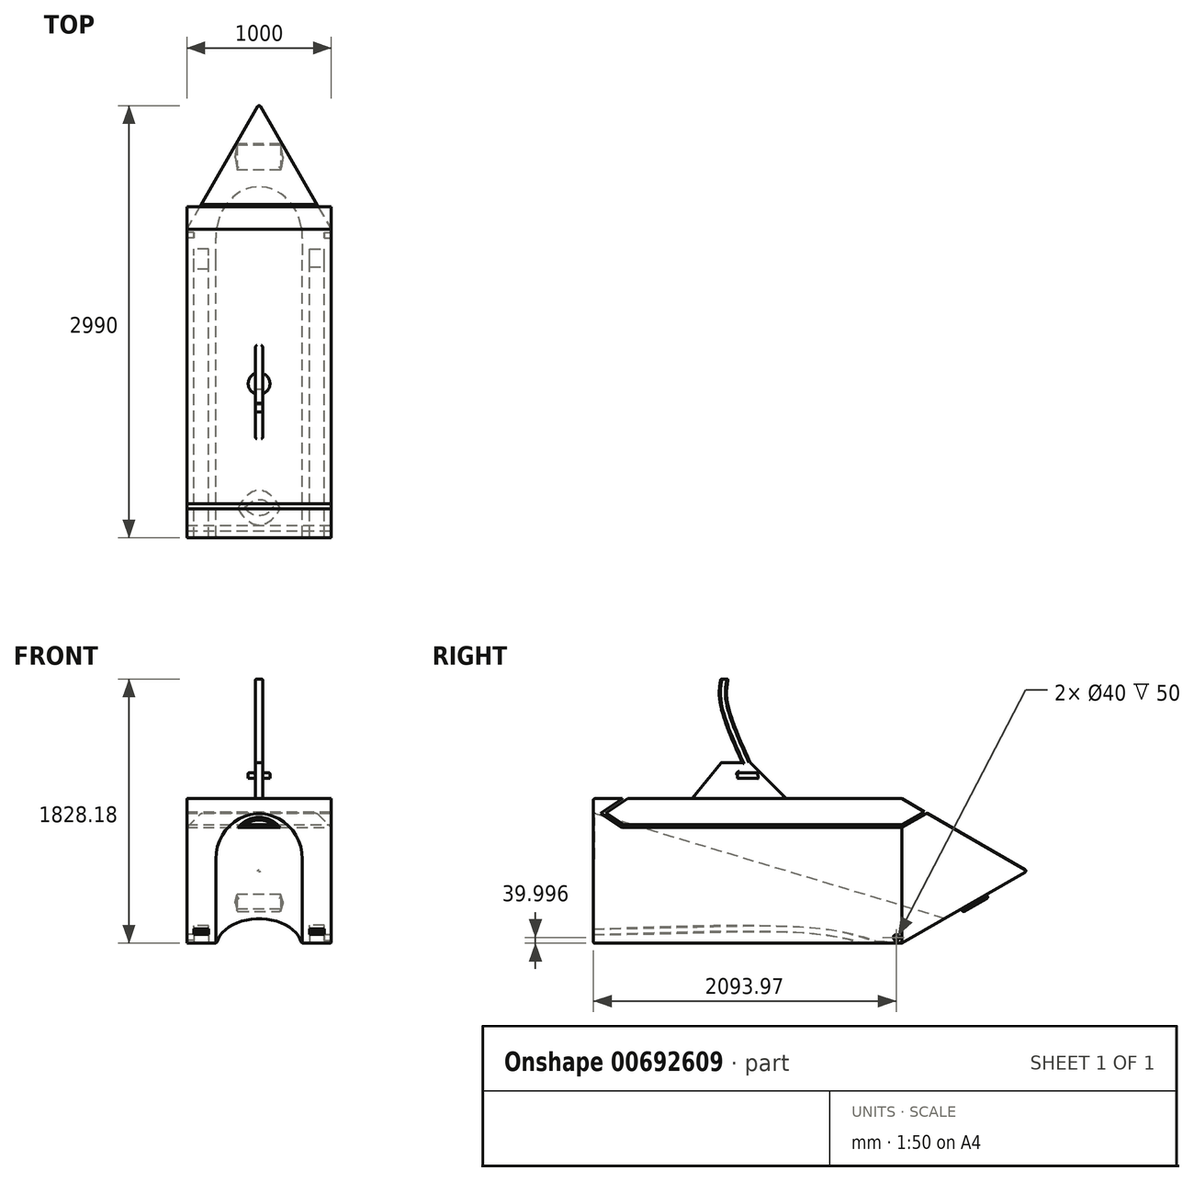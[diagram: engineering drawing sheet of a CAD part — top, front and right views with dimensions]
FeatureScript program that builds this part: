
annotation { "Feature Type Name" : "Feature", "Feature Type Description" : "" }
export const myFeature = defineFeature(function(context is Context, id is Id, definition is map)
    precondition{}
    {
        {
            var Q0;
            Q0=qCreatedBy(makeId("Front.planeOp"),FACE);
            var sketch = newSketch(context, id + "F0", { "sketchPlane" : qUnion([Q0])});
            skLineSegment(sketch, "E0.bottom", {"start": v(-515.88, 678.78) * mm, "end": v(484.12, 678.78) * mm});
            skLineSegment(sketch, "E0.top", {"start": v(-515.88, -321.22) * mm, "end": v(484.12, -321.22) * mm});
            skLineSegment(sketch, "E0.left", {"start": v(-515.88, 678.78) * mm, "end": v(-515.88, -321.22) * mm});
            skLineSegment(sketch, "E0.right", {"start": v(484.12, 678.78) * mm, "end": v(484.12, -321.22) * mm});
            skSolve(sketch);
        }
        {
            var Q0;
            Q0 = qSketchRegion(id + "F0", true);
            extrude(context, id + "F1", {"entities" : qUnion([Q0]), "depth" : 3000 * mm, "offsetDistance" : 25 * mm});
        }
        {
            var Q0;
            Q0=makeQuery(id+"F1.opExtrude","SWEPT_FACE",FACE,{"disambiguationData":[OSD([sQuery(id+"F0.wireOp",EDGE,"E0.right")])]});
            var sketch = newSketch(context, id + "F2", { "sketchPlane" : qUnion([Q0])});
            skLineSegment(sketch, "E1", {"start": v(-3000, 678.78) * mm, "end": v(-3000, 578.78) * mm});
            skLineSegment(sketch, "E2", {"start": v(0, 678.78) * mm, "end": v(0, -321.22) * mm});
            skLineSegment(sketch, "E3", {"start": v(-3000, 578.78) * mm, "end": v(0, -321.22) * mm});
            skLineSegment(sketch, "E4", {"start": v(0, -321.22) * mm, "end": v(0, -321.22) * mm});
            skSolve(sketch);
        }
        {
            var Q0;
            {var subQ0=sQuery(id+"F2.wireOp",EDGE,"E3");Q0=makeQuery(id+"F2.imprint","IMPRINT",FACE,{"disambiguationData":[TD([[makeQuery(id+"F2.imprint","IMPRINT",EDGE,{"derivedFrom":subQ0}),-1.0]])]});}
            extrude(context, id + "F3", {"entities" : qUnion([Q0]), "operationType" : NewBodyOperationType.REMOVE, "oppositeDirection" : true, "depth" : 800 * mm, "offsetDistance" : 25 * mm});
        }
        {
            var Q0;
            Q0=makeQuery(id+"F1.opExtrude","SWEPT_FACE",FACE,{"disambiguationData":[OSD([sQuery(id+"F0.wireOp",EDGE,"E0.bottom")])]});
            var sketch = newSketch(context, id + "F4", { "sketchPlane" : qUnion([Q0])});
            skLineSegment(sketch, "E5.bottom", {"start": v(484.12, -3000) * mm, "end": v(284.12, -3000) * mm});
            skLineSegment(sketch, "E5.top", {"start": v(484.12, 0) * mm, "end": v(284.12, 0) * mm});
            skLineSegment(sketch, "E5.left", {"start": v(484.12, -3000) * mm, "end": v(484.12, 0) * mm});
            skLineSegment(sketch, "E5.right", {"start": v(284.12, -3000) * mm, "end": v(284.12, 0) * mm});
            skSolve(sketch);
        }
        {
            var Q0;
            Q0 = qSketchRegion(id + "F4", true);
            extrude(context, id + "F5", {"entities" : qUnion([Q0]), "operationType" : NewBodyOperationType.ADD, "oppositeDirection" : true, "depth" : 1000 * mm, "offsetDistance" : 25 * mm});
        }
        {
            var Q0;
            Q0=makeQuery(id+"F3.boolean.opBoolean","COPY",EDGE,{"derivedFrom":makeQuery(id+"F3.opExtrude","CAP_EDGE",EDGE,{"disambiguationData":[OSD([sQuery(id+"F2.wireOp",EDGE,"E3")])],"isStart":false})});
            var Q1;
            Q1=makeQuery(id+"F5.boolean.opBoolean","INTERSECT",EDGE,{"derivedFrom":[makeQuery(id+"F3.boolean.opBoolean","COPY",FACE,{"derivedFrom":makeQuery(id+"F3.opExtrude","SWEPT_FACE",FACE,{"disambiguationData":[OSD([sQuery(id+"F2.wireOp",EDGE,"E3")])]})}),makeQuery(id+"F5.opExtrude","SWEPT_FACE",FACE,{"disambiguationData":[OSD([sQuery(id+"F4.wireOp",EDGE,"E5.right")])]})]});
            fillet(context, id + "F6", {"entities" : qUnion([Q0, Q1]), "radius" : 300 * mm, "tangentPropagation" : true, "allowEdgeOverflow" : false});
        }
        {
            var Q0;
            Q0=makeQuery(id+"F5.boolean.opBoolean","MERGE",FACE,{"derivedFrom":[makeQuery(id+"F1.opExtrude","SWEPT_FACE",FACE,{"disambiguationData":[OSD([sQuery(id+"F0.wireOp",EDGE,"E0.right")])]}),makeQuery(id+"F5.opExtrude","SWEPT_FACE",FACE,{"disambiguationData":[OSD([sQuery(id+"F4.wireOp",EDGE,"E5.left")])]})]});
            var sketch = newSketch(context, id + "F7", { "sketchPlane" : qUnion([Q0])});
            skLineSegment(sketch, "E6", {"start": v(0, 178.78) * mm, "end": v(-866.03, 678.78) * mm});
            skLineSegment(sketch, "E7", {"start": v(-866.03, 678.78) * mm, "end": v(0, 678.78) * mm});
            skLineSegment(sketch, "E8", {"start": v(0, 678.78) * mm, "end": v(0, 178.78) * mm});
            skLineSegment(sketch, "E9", {"start": v(0, 178.78) * mm, "end": v(-866.03, -321.22) * mm});
            skLineSegment(sketch, "E10", {"start": v(-866.03, -321.22) * mm, "end": v(0, -321.22) * mm});
            skLineSegment(sketch, "E11", {"start": v(0, -321.22) * mm, "end": v(0, 178.78) * mm});
            skSolve(sketch);
        }
        {
            var Q0;
            Q0 = qSketchRegion(id + "F7", true);
            extrude(context, id + "F8", {"entities" : qUnion([Q0]), "operationType" : NewBodyOperationType.REMOVE, "oppositeDirection" : true, "depth" : 1000 * mm, "offsetDistance" : 25 * mm});
        }
        {
            var Q0;
            Q0=makeQuery(id+"F1.opExtrude","SWEPT_FACE",FACE,{"disambiguationData":[OSD([sQuery(id+"F0.wireOp",EDGE,"E0.bottom")])]});
            var sketch = newSketch(context, id + "F9", { "sketchPlane" : qUnion([Q0])});
            skLineSegment(sketch, "E12", {"start": v(484.12, -866.03) * mm, "end": v(-15.88, -866.03) * mm});
            skLineSegment(sketch, "E13", {"start": v(-15.88, -866.03) * mm, "end": v(-15.88, 0) * mm});
            skLineSegment(sketch, "E14", {"start": v(-15.88, 0) * mm, "end": v(484.12, -866.03) * mm});
            skLineSegment(sketch, "E15", {"start": v(-515.88, -866.03) * mm, "end": v(-15.88, 0) * mm});
            skLineSegment(sketch, "E16", {"start": v(484.12, -866.03) * mm, "end": v(484.12, 0) * mm});
            skLineSegment(sketch, "E17", {"start": v(484.12, 0) * mm, "end": v(-15.88, 0) * mm});
            skLineSegment(sketch, "E18", {"start": v(-515.88, -866.03) * mm, "end": v(-515.88, 0) * mm});
            skLineSegment(sketch, "E19", {"start": v(-515.88, 0) * mm, "end": v(-15.88, 0) * mm});
            skSolve(sketch);
        }
        {
            var Q0;
            Q0=makeQuery(id+"F9.imprint","IMPRINT",FACE,{"disambiguationData":[TD([[makeQuery(id+"F9.imprint","IMPRINT",EDGE,{"derivedFrom":sQuery(id+"F9.wireOp",EDGE,"E14")}),1.0]])]});
            var Q1;
            Q1=makeQuery(id+"F9.imprint","IMPRINT",FACE,{"disambiguationData":[TD([[makeQuery(id+"F9.imprint","IMPRINT",EDGE,{"derivedFrom":sQuery(id+"F9.wireOp",EDGE,"E15")}),1.0]])]});
            extrude(context, id + "F10", {"entities" : qUnion([Q0, Q1]), "operationType" : NewBodyOperationType.REMOVE, "oppositeDirection" : true, "depth" : 1000 * mm, "offsetDistance" : 25 * mm});
        }
        {
            var Q0;
            Q0=makeQuery(id+"F5.boolean.opBoolean","MERGE",FACE,{"derivedFrom":[makeQuery(id+"F1.opExtrude","SWEPT_FACE",FACE,{"disambiguationData":[OSD([sQuery(id+"F0.wireOp",EDGE,"E0.right")])]}),makeQuery(id+"F5.opExtrude","SWEPT_FACE",FACE,{"disambiguationData":[OSD([sQuery(id+"F4.wireOp",EDGE,"E5.left")])]})]});
            var sketch = newSketch(context, id + "F11", { "sketchPlane" : qUnion([Q0])});
            skLineSegment(sketch, "E20", {"start": v(-3000, -321.22) * mm, "end": v(-3000, -221.22) * mm});
            skLineSegment(sketch, "E21", {"start": v(-3000, -321.22) * mm, "end": v(-1000, -321.22) * mm});
            skFitSpline(sketch, "E22", {"points": [v(-3000, -221.22) * mm, v(-1403.91, -221.22) * mm, v(-1000, -321.22) * mm], "startDerivative": vector(2813.55, 97.93) * mm, "endDerivative": vector(989.46, -345.85) * mm});
            skFitSpline(sketch, "E23.0", {"points": [v(-2998.6, -261.2) * mm, v(-2881.38, -257.12) * mm, v(-2705.6, -251) * mm, v(-2476.73, -244.16) * mm, v(-2309.2, -240) * mm, v(-2147.15, -237.17) * mm, v(-1991.93, -235.96) * mm, v(-1869.42, -236.59) * mm, v(-1776.22, -238.23) * mm, v(-1708.89, -240.06) * mm, v(-1644.32, -242.55) * mm, v(-1582.68, -245.72) * mm, v(-1524.16, -249.62) * mm, v(-1468.95, -254.27) * mm, v(-1425.85, -258.8) * mm, v(-1393.24, -262.83) * mm, v(-1361.79, -267.14) * mm, v(-1324.55, -273) * mm, v(-1282.84, -280.73) * mm, v(-1243.75, -289.07) * mm, v(-1206.92, -297.95) * mm, v(-1172, -307.3) * mm, v(-1127.47, -320.33) * mm, v(-1074.75, -337.47) * mm, v(-1033.81, -351.78) * mm, v(-1013.2, -358.98) * mm]});
            skLineSegment(sketch, "E24", {"start": v(-1013.2, -358.98) * mm, "end": v(-1000, -321.22) * mm});
            skLineSegment(sketch, "E25", {"start": v(-2998.6, -261.2) * mm, "end": v(-3000, -261.2) * mm});
            skLineSegment(sketch, "E26", {"start": v(-3000, -261.2) * mm, "end": v(-3000, -221.22) * mm});
            skSolve(sketch);
        }
        {
            var Q0;
            {var subQ4=sQuery(id+"F11.wireOp",EDGE,"E22");Q0=makeQuery(id+"F11.imprint","IMPRINT",FACE,{"disambiguationData":[TD([[makeQuery(id+"F11.imprint","IMPRINT",EDGE,{"derivedFrom":subQ4}),-1.0]])]});}
            extrude(context, id + "F12", {"entities" : qUnion([Q0]), "operationType" : NewBodyOperationType.REMOVE, "oppositeDirection" : true, "depth" : 150 * mm, "offsetDistance" : 25 * mm});
        }
        {
            var Q0;
            Q0 = qSketchRegion(id + "F11", true);
            extrude(context, id + "F13", {"entities" : qUnion([Q0]), "operationType" : NewBodyOperationType.ADD, "oppositeDirection" : true, "depth" : 50 * mm, "offsetDistance" : 25 * mm});
        }
        {
            var Q0;
            {var subQ0=sQuery(id+"F11.wireOp",EDGE,"E23.0");var subQ1=sQuery(id+"F11.wireOp",EDGE,"E22");var subQ2=sQuery(id+"F4.wireOp",EDGE,"E5.left");var subQ6=sQuery(id+"F0.wireOp",EDGE,"E0.right");var subQ7=sQuery(id+"F0.wireOp",EDGE,"E0.bottom");var subQ9=makeQuery(id+"F5.boolean.opBoolean","MERGE",FACE,{"derivedFrom":[makeQuery(id+"F1.opExtrude","SWEPT_FACE",FACE,{"disambiguationData":[OSD([subQ6])]}),makeQuery(id+"F5.opExtrude","SWEPT_FACE",FACE,{"disambiguationData":[OSD([subQ2])]})]});Q0=makeQuery(id+"F13.boolean.opBoolean","MERGE",FACE,{"derivedFrom":[makeQuery(id+"F12.boolean.opBoolean","SPLIT",FACE,{"disambiguationData":[TD([makeQuery(id+"F1.opExtrude","SWEPT_FACE",FACE,{"disambiguationData":[OSD([subQ7])]})])],"derivedFrom":subQ9}),makeQuery(id+"F12.boolean.opBoolean","SPLIT",FACE,{"disambiguationData":[TD([makeQuery(id+"F12.opExtrude","SWEPT_FACE",FACE,{"disambiguationData":[OSD([subQ0])]})])],"derivedFrom":subQ9}),makeQuery(id+"F13.opExtrude","CAP_FACE",FACE,{"disambiguationData":[OSD([sQuery(id+"F11.wireOp",EDGE,"E20"),sQuery(id+"F11.wireOp",EDGE,"E21"),subQ1,subQ0,sQuery(id+"F11.wireOp",EDGE,"E24"),sQuery(id+"F11.wireOp",EDGE,"E26")])],"isStart":true})]});}
            var sketch = newSketch(context, id + "F14", { "sketchPlane" : qUnion([Q0])});
            skLineSegment(sketch, "E27", {"start": v(-1125.47, -321.22) * mm, "end": v(-1000, -321.22) * mm});
            skLineSegment(sketch, "E28", {"start": v(-1000, -321.22) * mm, "end": v(-1013.2, -358.98) * mm});
            skLineSegment(sketch, "E29", {"start": v(-1013.2, -358.98) * mm, "end": v(-1125.47, -321.22) * mm});
            skSolve(sketch);
        }
        {
            var Q0;
            Q0 = qSketchRegion(id + "F14", true);
            extrude(context, id + "F15", {"entities" : qUnion([Q0]), "operationType" : NewBodyOperationType.REMOVE, "oppositeDirection" : true, "depth" : 50 * mm, "offsetDistance" : 25 * mm});
        }
        {
            var Q0;
            Q0=makeQuery(id+"F1.opExtrude","SWEPT_FACE",FACE,{"disambiguationData":[OSD([sQuery(id+"F0.wireOp",EDGE,"E0.left")])]});
            var sketch = newSketch(context, id + "F16", { "sketchPlane" : qUnion([Q0])});
            skLineSegment(sketch, "E30", {"start": v(3000, -321.22) * mm, "end": v(3000, -221.22) * mm});
            skLineSegment(sketch, "E31", {"start": v(3000, -321.22) * mm, "end": v(1000, -321.22) * mm});
            skFitSpline(sketch, "E32", {"points": [v(3000, -221.22) * mm, v(1404, -221.22) * mm, v(1000, -321.22) * mm], "startDerivative": vector(-2813.63, 8.94) * mm, "endDerivative": vector(-1014.58, -259.44) * mm});
            skFitSpline(sketch, "E33.0", {"points": [v(2999.87, -261.22) * mm, v(2882.3, -260.85) * mm, v(2705.99, -258.02) * mm, v(2476.49, -252.42) * mm, v(2308.53, -247.97) * mm, v(2146.13, -243.95) * mm, v(1990.68, -241.02) * mm, v(1868.1, -240.04) * mm, v(1774.93, -240.47) * mm, v(1707.68, -241.47) * mm, v(1643.25, -243.25) * mm, v(1581.82, -245.87) * mm, v(1523.58, -249.4) * mm, v(1477.89, -253.2) * mm, v(1443.13, -256.75) * mm, v(1417.99, -259.7) * mm, v(1393.81, -262.92) * mm, v(1370.5, -266.42) * mm, v(1348, -270.18) * mm, v(1319.03, -275.5) * mm, v(1284.61, -282.66) * mm, v(1245.8, -291.9) * mm, v(1209.05, -301.62) * mm, v(1173.98, -311.65) * mm, v(1140.18, -321.81) * mm, v(1107.27, -331.93) * mm, v(1074.85, -341.83) * mm, v(1042.55, -351.3) * mm, v(1020.85, -357.18) * mm, v(1009.9, -359.98) * mm]});
            skLineSegment(sketch, "E34", {"start": v(1000, -321.22) * mm, "end": v(1009.9, -359.98) * mm});
            skLineSegment(sketch, "E35", {"start": v(2999.87, -261.22) * mm, "end": v(3000, -261.22) * mm});
            skLineSegment(sketch, "E36", {"start": v(3000, -261.22) * mm, "end": v(3000, -221.22) * mm});
            skSolve(sketch);
        }
        {
            var Q0;
            {var subQ4=sQuery(id+"F16.wireOp",EDGE,"E32");Q0=makeQuery(id+"F16.imprint","IMPRINT",FACE,{"disambiguationData":[TD([[makeQuery(id+"F16.imprint","IMPRINT",EDGE,{"derivedFrom":subQ4}),1.0]])]});}
            extrude(context, id + "F17", {"entities" : qUnion([Q0]), "operationType" : NewBodyOperationType.REMOVE, "oppositeDirection" : true, "depth" : 150 * mm, "offsetDistance" : 25 * mm});
        }
        {
            var Q0;
            Q0 = qSketchRegion(id + "F16", true);
            extrude(context, id + "F18", {"entities" : qUnion([Q0]), "operationType" : NewBodyOperationType.ADD, "oppositeDirection" : true, "depth" : 50 * mm, "offsetDistance" : 25 * mm});
        }
        {
            var Q0;
            {var subQ0=sQuery(id+"F16.wireOp",EDGE,"E33.0");var subQ1=sQuery(id+"F16.wireOp",EDGE,"E32");var subQ3=sQuery(id+"F0.wireOp",EDGE,"E0.left");var subQ5=sQuery(id+"F0.wireOp",EDGE,"E0.bottom");var subQ9=makeQuery(id+"F1.opExtrude","SWEPT_FACE",FACE,{"disambiguationData":[OSD([subQ3])]});Q0=makeQuery(id+"F18.boolean.opBoolean","MERGE",FACE,{"derivedFrom":[makeQuery(id+"F17.boolean.opBoolean","SPLIT",FACE,{"disambiguationData":[TD([makeQuery(id+"F1.opExtrude","SWEPT_FACE",FACE,{"disambiguationData":[OSD([subQ5])]})])],"derivedFrom":subQ9}),makeQuery(id+"F17.boolean.opBoolean","SPLIT",FACE,{"disambiguationData":[TD([makeQuery(id+"F17.opExtrude","SWEPT_FACE",FACE,{"disambiguationData":[OSD([subQ0])]})])],"derivedFrom":subQ9}),makeQuery(id+"F18.opExtrude","CAP_FACE",FACE,{"disambiguationData":[OSD([sQuery(id+"F16.wireOp",EDGE,"E30"),sQuery(id+"F16.wireOp",EDGE,"E31"),subQ1,subQ0,sQuery(id+"F16.wireOp",EDGE,"E34"),sQuery(id+"F16.wireOp",EDGE,"E36")])],"isStart":true})]});}
            var sketch = newSketch(context, id + "F19", { "sketchPlane" : qUnion([Q0])});
            skLineSegment(sketch, "E37", {"start": v(1142.24, -321.22) * mm, "end": v(1000, -321.22) * mm});
            skLineSegment(sketch, "E38", {"start": v(1000, -321.22) * mm, "end": v(1009.9, -359.98) * mm});
            skLineSegment(sketch, "E39", {"start": v(1009.9, -359.98) * mm, "end": v(1020.33, -366.43) * mm});
            skLineSegment(sketch, "E40", {"start": v(1020.33, -366.43) * mm, "end": v(1142.24, -321.22) * mm});
            skSolve(sketch);
        }
        {
            var Q0;
            Q0 = qSketchRegion(id + "F19", true);
            extrude(context, id + "F20", {"entities" : qUnion([Q0]), "operationType" : NewBodyOperationType.REMOVE, "oppositeDirection" : true, "depth" : 50 * mm, "offsetDistance" : 25 * mm});
        }
        {
            var Q0;
            {var subQ0=sQuery(id+"F16.wireOp",EDGE,"E33.0");var subQ1=sQuery(id+"F16.wireOp",EDGE,"E32");var subQ3=sQuery(id+"F0.wireOp",EDGE,"E0.left");var subQ5=sQuery(id+"F0.wireOp",EDGE,"E0.bottom");var subQ9=makeQuery(id+"F1.opExtrude","SWEPT_FACE",FACE,{"disambiguationData":[OSD([subQ3])]});Q0=makeQuery(id+"F18.boolean.opBoolean","MERGE",FACE,{"derivedFrom":[makeQuery(id+"F17.boolean.opBoolean","SPLIT",FACE,{"disambiguationData":[TD([makeQuery(id+"F1.opExtrude","SWEPT_FACE",FACE,{"disambiguationData":[OSD([subQ5])]})])],"derivedFrom":subQ9}),makeQuery(id+"F17.boolean.opBoolean","SPLIT",FACE,{"disambiguationData":[TD([makeQuery(id+"F17.opExtrude","SWEPT_FACE",FACE,{"disambiguationData":[OSD([subQ0])]})])],"derivedFrom":subQ9}),makeQuery(id+"F18.opExtrude","CAP_FACE",FACE,{"disambiguationData":[OSD([sQuery(id+"F16.wireOp",EDGE,"E30"),sQuery(id+"F16.wireOp",EDGE,"E31"),subQ1,subQ0,sQuery(id+"F16.wireOp",EDGE,"E34"),sQuery(id+"F16.wireOp",EDGE,"E36")])],"isStart":true})]});}
            var sketch = newSketch(context, id + "F21", { "sketchPlane" : qUnion([Q0])});
            skCircle(sketch, "E41", {"center": v(906.03, -281.22) * mm, "radius": 20 * mm});
            skSolve(sketch);
        }
        {
            var Q0;
            Q0 = qSketchRegion(id + "F21", true);
            extrude(context, id + "F22", {"entities" : qUnion([Q0]), "operationType" : NewBodyOperationType.REMOVE, "oppositeDirection" : true, "depth" : 50 * mm, "offsetDistance" : 25 * mm});
        }
        {
            var Q0;
            {var subQ0=sQuery(id+"F11.wireOp",EDGE,"E23.0");var subQ1=sQuery(id+"F11.wireOp",EDGE,"E22");var subQ2=sQuery(id+"F4.wireOp",EDGE,"E5.left");var subQ6=sQuery(id+"F0.wireOp",EDGE,"E0.right");var subQ7=sQuery(id+"F0.wireOp",EDGE,"E0.bottom");var subQ9=makeQuery(id+"F5.boolean.opBoolean","MERGE",FACE,{"derivedFrom":[makeQuery(id+"F1.opExtrude","SWEPT_FACE",FACE,{"disambiguationData":[OSD([subQ6])]}),makeQuery(id+"F5.opExtrude","SWEPT_FACE",FACE,{"disambiguationData":[OSD([subQ2])]})]});Q0=makeQuery(id+"F13.boolean.opBoolean","MERGE",FACE,{"derivedFrom":[makeQuery(id+"F12.boolean.opBoolean","SPLIT",FACE,{"disambiguationData":[TD([makeQuery(id+"F1.opExtrude","SWEPT_FACE",FACE,{"disambiguationData":[OSD([subQ7])]})])],"derivedFrom":subQ9}),makeQuery(id+"F12.boolean.opBoolean","SPLIT",FACE,{"disambiguationData":[TD([makeQuery(id+"F12.opExtrude","SWEPT_FACE",FACE,{"disambiguationData":[OSD([subQ0])]})])],"derivedFrom":subQ9}),makeQuery(id+"F13.opExtrude","CAP_FACE",FACE,{"disambiguationData":[OSD([sQuery(id+"F11.wireOp",EDGE,"E20"),sQuery(id+"F11.wireOp",EDGE,"E21"),subQ1,subQ0,sQuery(id+"F11.wireOp",EDGE,"E24"),sQuery(id+"F11.wireOp",EDGE,"E26")])],"isStart":true})]});}
            var sketch = newSketch(context, id + "F23", { "sketchPlane" : qUnion([Q0])});
            skCircle(sketch, "E42", {"center": v(-906.03, -281.22) * mm, "radius": 20 * mm});
            skSolve(sketch);
        }
        {
            var Q0;
            Q0 = qSketchRegion(id + "F23", true);
            extrude(context, id + "F24", {"entities" : qUnion([Q0]), "operationType" : NewBodyOperationType.REMOVE, "oppositeDirection" : true, "depth" : 50 * mm, "offsetDistance" : 25 * mm});
        }
        {
            var Q0;
            Q0=makeQuery(id+"F8.boolean.opBoolean","COPY",FACE,{"derivedFrom":makeQuery(id+"F8.opExtrude","SWEPT_FACE",FACE,{"disambiguationData":[OSD([sQuery(id+"F7.wireOp",EDGE,"E9")])]})});
            var sketch = newSketch(context, id + "F25", { "sketchPlane" : qUnion([Q0])});
            skLineSegment(sketch, "E43.bottom", {"start": v(133.3, 236.82) * mm, "end": v(-166.7, 236.82) * mm});
            skLineSegment(sketch, "E43.top", {"start": v(133.3, 436.82) * mm, "end": v(-166.7, 436.82) * mm});
            skLineSegment(sketch, "E43.left", {"start": v(133.3, 236.82) * mm, "end": v(133.3, 436.82) * mm});
            skLineSegment(sketch, "E43.right", {"start": v(-166.7, 236.82) * mm, "end": v(-166.7, 436.82) * mm});
            skLineSegment(sketch, "E44", {"start": v(-166.7, 336.82) * mm, "end": v(-181.7, 336.82) * mm});
            skLineSegment(sketch, "E45", {"start": v(-181.7, 336.82) * mm, "end": v(-166.7, 236.82) * mm});
            skLineSegment(sketch, "E46", {"start": v(-181.7, 336.82) * mm, "end": v(-166.7, 436.82) * mm});
            skLineSegment(sketch, "E47", {"start": v(133.3, 336.82) * mm, "end": v(148.3, 336.82) * mm});
            skLineSegment(sketch, "E48", {"start": v(148.3, 336.82) * mm, "end": v(133.3, 236.82) * mm});
            skLineSegment(sketch, "E49", {"start": v(148.3, 336.82) * mm, "end": v(133.3, 436.82) * mm});
            skSolve(sketch);
        }
        {
            var Q0;
            {var subQ3=sQuery(id+"F25.wireOp",EDGE,"E43.bottom");Q0=makeQuery(id+"F25.imprint","IMPRINT",FACE,{"disambiguationData":[TD([[makeQuery(id+"F25.imprint","IMPRINT",EDGE,{"derivedFrom":subQ3}),-1.0]])]});}
            extrude(context, id + "F26", {"entities" : qUnion([Q0]), "operationType" : NewBodyOperationType.ADD, "depth" : 25 * mm, "offsetDistance" : 25 * mm});
        }
        {
            var Q0;
            {var subQ2=sQuery(id+"F25.wireOp",EDGE,"E47");Q0=makeQuery(id+"F25.imprint","IMPRINT",FACE,{"disambiguationData":[TD([[makeQuery(id+"F25.imprint","IMPRINT",EDGE,{"derivedFrom":subQ2}),-1.0]])]});}
            var Q1;
            {var subQ2=sQuery(id+"F25.wireOp",EDGE,"E47");Q1=makeQuery(id+"F25.imprint","IMPRINT",FACE,{"disambiguationData":[TD([[makeQuery(id+"F25.imprint","IMPRINT",EDGE,{"derivedFrom":subQ2}),1.0]])]});}
            var Q2;
            {var subQ2=sQuery(id+"F25.wireOp",EDGE,"E44");Q2=makeQuery(id+"F25.imprint","IMPRINT",FACE,{"disambiguationData":[TD([[makeQuery(id+"F25.imprint","IMPRINT",EDGE,{"derivedFrom":subQ2}),1.0]])]});}
            var Q3;
            {var subQ2=sQuery(id+"F25.wireOp",EDGE,"E44");Q3=makeQuery(id+"F25.imprint","IMPRINT",FACE,{"disambiguationData":[TD([[makeQuery(id+"F25.imprint","IMPRINT",EDGE,{"derivedFrom":subQ2}),-1.0]])]});}
            extrude(context, id + "F27", {"entities" : qUnion([Q0, Q1, Q2, Q3]), "operationType" : NewBodyOperationType.ADD, "depth" : 10 * mm, "offsetDistance" : 25 * mm});
        }
        {
            var Q0;
            Q0=makeQuery(id+"F1.opExtrude","SWEPT_FACE",FACE,{"disambiguationData":[OSD([sQuery(id+"F0.wireOp",EDGE,"E0.bottom")])]});
            var sketch = newSketch(context, id + "F28", { "sketchPlane" : qUnion([Q0])});
            skLineSegment(sketch, "E50.bottom", {"start": v(-40.88, -1666.03) * mm, "end": v(9.12, -1666.03) * mm});
            skLineSegment(sketch, "E50.top", {"start": v(-40.88, -2066.03) * mm, "end": v(9.12, -2066.03) * mm});
            skLineSegment(sketch, "E50.left", {"start": v(-40.88, -1666.03) * mm, "end": v(-40.88, -2066.03) * mm});
            skLineSegment(sketch, "E50.right", {"start": v(9.12, -1666.03) * mm, "end": v(9.12, -2066.03) * mm});
            skSolve(sketch);
        }
        {
            var Q0;
            Q0 = qSketchRegion(id + "F28", true);
            extrude(context, id + "F29", {"entities" : qUnion([Q0]), "operationType" : NewBodyOperationType.ADD, "depth" : 250 * mm, "offsetDistance" : 25 * mm});
        }
        {
            var Q0;
            Q0=makeQuery(id+"F29.opExtrude","CAP_EDGE",EDGE,{"disambiguationData":[OSD([sQuery(id+"F28.wireOp",EDGE,"E50.bottom")])],"isStart":false});
            chamfer(context, id + "F30", {"entities" : qUnion([Q0]), "chamferType" : ChamferType.TWO_OFFSETS, "width1" : 250 * mm, "oppositeDirection" : false, "width2" : 250 * mm, "tangentPropagation" : true});
        }
        {
            var Q0;
            Q0=makeQuery(id+"F29.opExtrude","SWEPT_FACE",FACE,{"disambiguationData":[OSD([sQuery(id+"F28.wireOp",EDGE,"E50.top")])]});
            var sketch = newSketch(context, id + "F31", { "sketchPlane" : qUnion([Q0])});
            skLineSegment(sketch, "E51.bottom", {"start": v(-40.88, 928.78) * mm, "end": v(9.12, 928.78) * mm});
            skLineSegment(sketch, "E51.top", {"start": v(-40.88, 678.78) * mm, "end": v(9.12, 678.78) * mm});
            skLineSegment(sketch, "E51.left", {"start": v(-40.88, 928.78) * mm, "end": v(-40.88, 678.78) * mm});
            skLineSegment(sketch, "E51.right", {"start": v(9.12, 928.78) * mm, "end": v(9.12, 678.78) * mm});
            skSolve(sketch);
        }
        {
            var Q0;
            Q0 = qSketchRegion(id + "F31", true);
            extrude(context, id + "F32", {"entities" : qUnion([Q0]), "operationType" : NewBodyOperationType.ADD, "depth" : 250 * mm, "offsetDistance" : 25 * mm});
        }
        {
            var Q0;
            Q0=makeQuery(id+"F32.opExtrude","CAP_EDGE",EDGE,{"disambiguationData":[OSD([sQuery(id+"F31.wireOp",EDGE,"E51.bottom")])],"isStart":false});
            chamfer(context, id + "F33", {"entities" : qUnion([Q0]), "chamferType" : ChamferType.TWO_OFFSETS, "width1" : 200 * mm, "oppositeDirection" : false, "width2" : 250 * mm, "tangentPropagation" : true});
        }
        {
            var Q0;
            Q0=makeQuery(id+"F1.opExtrude","SWEPT_FACE",FACE,{"disambiguationData":[OSD([sQuery(id+"F0.wireOp",EDGE,"E0.bottom")])]});
            var sketch = newSketch(context, id + "F34", { "sketchPlane" : qUnion([Q0])});
            skLineSegment(sketch, "E52", {"start": v(484.12, -1933.01) * mm, "end": v(-515.88, -1933.01) * mm});
            skCircle(sketch, "E53", {"center": v(-15.88, -1933.01) * mm, "radius": 75 * mm});
            skSolve(sketch);
        }
        {
            var Q0;
            Q0 = qSketchRegion(id + "F34", true);
            extrude(context, id + "F35", {"entities" : qUnion([Q0]), "operationType" : NewBodyOperationType.ADD, "depth" : 180 * mm, "offsetDistance" : 25 * mm});
        }
        {
            var Q0;
            Q0 = qSketchRegion(id + "F34", true);
            extrude(context, id + "F36", {"entities" : qUnion([Q0]), "operationType" : NewBodyOperationType.REMOVE, "depth" : 140 * mm, "offsetDistance" : 25 * mm});
        }
        {
            var Q0;
            Q0=makeQuery(id+"F32.boolean.opBoolean","MERGE",FACE,{"derivedFrom":[makeQuery(id+"F29.opExtrude","SWEPT_FACE",FACE,{"disambiguationData":[OSD([sQuery(id+"F28.wireOp",EDGE,"E50.right")])]}),makeQuery(id+"F32.opExtrude","SWEPT_FACE",FACE,{"disambiguationData":[OSD([sQuery(id+"F31.wireOp",EDGE,"E51.right")])]})]});
            var sketch = newSketch(context, id + "F37", { "sketchPlane" : qUnion([Q0])});
            skLineSegment(sketch, "E54.bottom", {"start": v(-2027.55, 678.78) * mm, "end": v(-1844.65, 678.78) * mm});
            skLineSegment(sketch, "E54.top", {"start": v(-2027.55, 818.78) * mm, "end": v(-1844.65, 818.78) * mm});
            skLineSegment(sketch, "E54.left", {"start": v(-2027.55, 678.78) * mm, "end": v(-2027.55, 818.78) * mm});
            skLineSegment(sketch, "E54.right", {"start": v(-1844.65, 678.78) * mm, "end": v(-1844.65, 818.78) * mm});
            skSolve(sketch);
        }
        {
            var Q0;
            Q0 = qSketchRegion(id + "F37", true);
            extrude(context, id + "F38", {"entities" : qUnion([Q0]), "operationType" : NewBodyOperationType.ADD, "oppositeDirection" : true, "depth" : 50 * mm, "offsetDistance" : 25 * mm});
        }
        {
            var Q0;
            Q0=makeQuery(id+"F38.boolean.opBoolean","MERGE",FACE,{"derivedFrom":[makeQuery(id+"F32.boolean.opBoolean","MERGE",FACE,{"derivedFrom":[makeQuery(id+"F29.opExtrude","SWEPT_FACE",FACE,{"disambiguationData":[OSD([sQuery(id+"F28.wireOp",EDGE,"E50.right")])]}),makeQuery(id+"F32.opExtrude","SWEPT_FACE",FACE,{"disambiguationData":[OSD([sQuery(id+"F31.wireOp",EDGE,"E51.right")])]})]}),makeQuery(id+"F38.opExtrude","CAP_FACE",FACE,{"disambiguationData":[OSD([sQuery(id+"F37.wireOp",EDGE,"E54.bottom"),sQuery(id+"F37.wireOp",EDGE,"E54.top"),sQuery(id+"F37.wireOp",EDGE,"E54.left"),sQuery(id+"F37.wireOp",EDGE,"E54.right")])],"isStart":true})]});
            var sketch = newSketch(context, id + "F39", { "sketchPlane" : qUnion([Q0])});
            skFitSpline(sketch, "E55", {"points": [v(-2068.08, 1506.96) * mm, v(-2074.79, 1352.65) * mm, v(-1916.03, 928.78) * mm], "startDerivative": vector(-67.92, -371.81) * mm, "endDerivative": vector(336.63, -751.35) * mm});
            skFitSpline(sketch, "E56.0", {"points": [v(-2117.27, 1515.94) * mm, v(-2118.68, 1508.2) * mm, v(-2121.6, 1492.27) * mm, v(-2125.6, 1466.65) * mm, v(-2128.08, 1443.57) * mm, v(-2129.16, 1423.96) * mm, v(-2129.45, 1408.67) * mm, v(-2129.12, 1392.78) * mm, v(-2128.27, 1379.02) * mm, v(-2127.21, 1367.7) * mm, v(-2126.22, 1359.04) * mm, v(-2125.22, 1351.68) * mm, v(-2124.32, 1345.72) * mm, v(-2123.35, 1339.7) * mm, v(-2122, 1332.11) * mm, v(-2119.6, 1319.83) * mm, v(-2116.11, 1304.21) * mm, v(-2111.24, 1285.02) * mm, v(-2105.71, 1265.39) * mm, v(-2099.59, 1245.32) * mm, v(-2090.66, 1218) * mm, v(-2078.2, 1182.86) * mm, v(-2061.44, 1139.26) * mm, v(-2043.21, 1094.46) * mm, v(-2023.81, 1048.7) * mm, v(-1996.79, 986.74) * mm, v(-1975.68, 939.64) * mm, v(-1961.65, 908.33) * mm]});
            skLineSegment(sketch, "E57", {"start": v(-2068.08, 1506.96) * mm, "end": v(-2125.83, 1506.96) * mm});
            skLineSegment(sketch, "E58", {"start": v(-1916.03, 928.78) * mm, "end": v(-1970.81, 928.78) * mm});
            skSolve(sketch);
        }
        {
            var Q0;
            Q0 = qSketchRegion(id + "F39", true);
            extrude(context, id + "F40", {"entities" : qUnion([Q0]), "operationType" : NewBodyOperationType.ADD, "oppositeDirection" : true, "depth" : 50 * mm, "offsetDistance" : 25 * mm});
        }
        {
            var Q0;
            {var subQ0=sQuery(id+"F11.wireOp",EDGE,"E23.0");var subQ1=sQuery(id+"F11.wireOp",EDGE,"E22");var subQ2=sQuery(id+"F4.wireOp",EDGE,"E5.left");var subQ6=sQuery(id+"F0.wireOp",EDGE,"E0.right");var subQ7=sQuery(id+"F0.wireOp",EDGE,"E0.bottom");var subQ9=makeQuery(id+"F5.boolean.opBoolean","MERGE",FACE,{"derivedFrom":[makeQuery(id+"F1.opExtrude","SWEPT_FACE",FACE,{"disambiguationData":[OSD([subQ6])]}),makeQuery(id+"F5.opExtrude","SWEPT_FACE",FACE,{"disambiguationData":[OSD([subQ2])]})]});Q0=makeQuery(id+"F13.boolean.opBoolean","MERGE",FACE,{"derivedFrom":[makeQuery(id+"F12.boolean.opBoolean","SPLIT",FACE,{"disambiguationData":[TD([makeQuery(id+"F1.opExtrude","SWEPT_FACE",FACE,{"disambiguationData":[OSD([subQ7])]})])],"derivedFrom":subQ9}),makeQuery(id+"F12.boolean.opBoolean","SPLIT",FACE,{"disambiguationData":[TD([makeQuery(id+"F12.opExtrude","SWEPT_FACE",FACE,{"disambiguationData":[OSD([subQ0])]})])],"derivedFrom":subQ9}),makeQuery(id+"F13.opExtrude","CAP_FACE",FACE,{"disambiguationData":[OSD([sQuery(id+"F11.wireOp",EDGE,"E20"),sQuery(id+"F11.wireOp",EDGE,"E21"),subQ1,subQ0,sQuery(id+"F11.wireOp",EDGE,"E24"),sQuery(id+"F11.wireOp",EDGE,"E26")])],"isStart":true})]});}
            var sketch = newSketch(context, id + "F41", { "sketchPlane" : qUnion([Q0])});
            skLineSegment(sketch, "E59", {"start": v(-3000, 678.78) * mm, "end": v(-2800, 678.78) * mm});
            skLineSegment(sketch, "E60", {"start": v(-3000, 678.78) * mm, "end": v(-3000, 578.78) * mm});
            skLineSegment(sketch, "E61", {"start": v(-3000, 578.78) * mm, "end": v(-2950, 578.78) * mm});
            skLineSegment(sketch, "E62", {"start": v(-2800, 678.78) * mm, "end": v(-2950, 578.78) * mm});
            skLineSegment(sketch, "E63.MirrorCS", {"start": v(-2800, 478.78) * mm, "end": v(-2950, 578.78) * mm});
            skLineSegment(sketch, "E64", {"start": v(-2800, 478.78) * mm, "end": v(-866.03, 478.78) * mm});
            skLineSegment(sketch, "E65", {"start": v(-866.03, 478.78) * mm, "end": v(-692.6, 578.78) * mm});
            skLineSegment(sketch, "E66", {"start": v(-692.6, 578.78) * mm, "end": v(-866.03, 678.78) * mm});
            skLineSegment(sketch, "E67.0", {"start": v(-2793.94, 498.78) * mm, "end": v(-866.03, 498.78) * mm});
            skLineSegment(sketch, "E67.1", {"start": v(-2793.94, 498.78) * mm, "end": v(-2913.94, 578.78) * mm});
            skLineSegment(sketch, "E67.2", {"start": v(-2788.9, 662.13) * mm, "end": v(-2913.94, 578.78) * mm});
            skLineSegment(sketch, "E68", {"start": v(-2788.9, 662.13) * mm, "end": v(-2763.94, 678.78) * mm});
            skLineSegment(sketch, "E69", {"start": v(-2763.94, 678.78) * mm, "end": v(-2800, 678.78) * mm});
            skLineSegment(sketch, "E70", {"start": v(-866.03, 498.78) * mm, "end": v(-709.95, 588.78) * mm});
            skSolve(sketch);
        }
        {
            var Q0;
            {var subQ5=sQuery(id+"F41.wireOp",EDGE,"E70");Q0=makeQuery(id+"F41.imprint","IMPRINT",FACE,{"disambiguationData":[TD([[makeQuery(id+"F41.imprint","IMPRINT",EDGE,{"derivedFrom":subQ5}),1.0]])]});}
            extrude(context, id + "F42", {"entities" : qUnion([Q0]), "operationType" : NewBodyOperationType.ADD, "oppositeDirection" : true, "depth" : 1000 * mm, "offsetDistance" : 25 * mm});
        }
        {
            var Q0;
            Q0=makeQuery(id+"F41.imprint","IMPRINT",FACE,{"disambiguationData":[TD([[makeQuery(id+"F41.imprint","IMPRINT",EDGE,{"derivedFrom":sQuery(id+"F41.wireOp",EDGE,"E62")}),1.0]])]});
            extrude(context, id + "F43", {"entities" : qUnion([Q0]), "operationType" : NewBodyOperationType.REMOVE, "oppositeDirection" : true, "depth" : 1000 * mm, "offsetDistance" : 25 * mm});
        }
        {
            var Q0;
            {var subQ0=sQuery(id+"F41.wireOp",EDGE,"E65");Q0=makeQuery(id+"F41.imprint","IMPRINT",FACE,{"disambiguationData":[TD([[makeQuery(id+"F41.imprint","IMPRINT",EDGE,{"derivedFrom":subQ0}),1.0]])]});}
            extrude(context, id + "F44", {"entities" : qUnion([Q0]), "operationType" : NewBodyOperationType.REMOVE, "oppositeDirection" : true, "depth" : 1000 * mm, "offsetDistance" : 25 * mm});
        }
        {
            var Q0;
            Q0=makeQuery(id+"F10.boolean.opBoolean","INTERSECT",EDGE,{"derivedFrom":[makeQuery(id+"F8.boolean.opBoolean","COPY",FACE,{"derivedFrom":makeQuery(id+"F8.opExtrude","SWEPT_FACE",FACE,{"disambiguationData":[OSD([sQuery(id+"F7.wireOp",EDGE,"E6")])]})}),makeQuery(id+"F10.opExtrude","SWEPT_FACE",FACE,{"disambiguationData":[OSD([sQuery(id+"F9.wireOp",EDGE,"E14")])]})]});
            var Q1;
            Q1=makeQuery(id+"F10.boolean.opBoolean","INTERSECT",EDGE,{"derivedFrom":[makeQuery(id+"F8.boolean.opBoolean","COPY",FACE,{"derivedFrom":makeQuery(id+"F8.opExtrude","SWEPT_FACE",FACE,{"disambiguationData":[OSD([sQuery(id+"F7.wireOp",EDGE,"E6")])]})}),makeQuery(id+"F10.opExtrude","SWEPT_FACE",FACE,{"disambiguationData":[OSD([sQuery(id+"F9.wireOp",EDGE,"E15")])]})]});
            var Q2;
            Q2=makeQuery(id+"F10.boolean.opBoolean","INTERSECT",EDGE,{"derivedFrom":[makeQuery(id+"F8.boolean.opBoolean","COPY",FACE,{"derivedFrom":makeQuery(id+"F8.opExtrude","SWEPT_FACE",FACE,{"disambiguationData":[OSD([sQuery(id+"F7.wireOp",EDGE,"E9")])]})}),makeQuery(id+"F10.opExtrude","SWEPT_FACE",FACE,{"disambiguationData":[OSD([sQuery(id+"F9.wireOp",EDGE,"E15")])]})]});
            var Q3;
            Q3=makeQuery(id+"F10.boolean.opBoolean","INTERSECT",EDGE,{"derivedFrom":[makeQuery(id+"F8.boolean.opBoolean","COPY",FACE,{"derivedFrom":makeQuery(id+"F8.opExtrude","SWEPT_FACE",FACE,{"disambiguationData":[OSD([sQuery(id+"F7.wireOp",EDGE,"E9")])]})}),makeQuery(id+"F10.opExtrude","SWEPT_FACE",FACE,{"disambiguationData":[OSD([sQuery(id+"F9.wireOp",EDGE,"E14")])]})]});
            fillet(context, id + "F45", {"entities" : qUnion([Q0, Q1, Q2, Q3]), "radius" : 10 * mm, "tangentPropagation" : true, "allowEdgeOverflow" : false});
        }
        {
            var Q0;
            Q0=makeQuery(id+"F40.opExtrude","CAP_EDGE",EDGE,{"disambiguationData":[OSD([sQuery(id+"F39.wireOp",EDGE,"E55")])],"isStart":true});
            var Q1;
            Q1=makeQuery(id+"F40.opExtrude","CAP_EDGE",EDGE,{"disambiguationData":[OSD([sQuery(id+"F39.wireOp",EDGE,"E55")])],"isStart":false});
            var Q2;
            Q2=makeQuery(id+"F30.opChamfer","BLEND_EDGE",EDGE,{"blendedFrom":[makeQuery(id+"F29.opExtrude","CAP_EDGE",EDGE,{"disambiguationData":[OSD([sQuery(id+"F28.wireOp",EDGE,"E50.bottom")])],"isStart":false}),makeQuery(id+"F29.opExtrude","SWEPT_FACE",FACE,{"disambiguationData":[OSD([sQuery(id+"F28.wireOp",EDGE,"E50.left")])]})],"blendedInto":[makeQuery(id+"F29.opExtrude","SWEPT_FACE",FACE,{"disambiguationData":[OSD([sQuery(id+"F28.wireOp",EDGE,"E50.left")])]})]});
            var Q3;
            Q3=makeQuery(id+"F30.opChamfer","BLEND_EDGE",EDGE,{"blendedFrom":[makeQuery(id+"F29.opExtrude","CAP_EDGE",EDGE,{"disambiguationData":[OSD([sQuery(id+"F28.wireOp",EDGE,"E50.bottom")])],"isStart":false}),makeQuery(id+"F29.opExtrude","SWEPT_FACE",FACE,{"disambiguationData":[OSD([sQuery(id+"F28.wireOp",EDGE,"E50.right")])]})],"blendedInto":[makeQuery(id+"F29.opExtrude","SWEPT_FACE",FACE,{"disambiguationData":[OSD([sQuery(id+"F28.wireOp",EDGE,"E50.right")])]})]});
            var Q4;
            {var subQ0=sQuery(id+"F28.wireOp",EDGE,"E50.right");var subQ1=sQuery(id+"F28.wireOp",EDGE,"E50.bottom");Q4=makeQuery(id+"F40.boolean.opBoolean","MERGE",EDGE,{"derivedFrom":[makeQuery(id+"F30.opChamfer","BLEND_EDGE",EDGE,{"blendedFrom":[makeQuery(id+"F29.opExtrude","CAP_EDGE",EDGE,{"disambiguationData":[OSD([subQ1])],"isStart":false}),makeQuery(id+"F29.opExtrude","CAP_FACE",FACE,{"disambiguationData":[OSD([subQ1,sQuery(id+"F28.wireOp",EDGE,"E50.top"),sQuery(id+"F28.wireOp",EDGE,"E50.left"),subQ0])],"isStart":false})],"blendedInto":[makeQuery(id+"F29.opExtrude","CAP_FACE",FACE,{"disambiguationData":[OSD([subQ1,sQuery(id+"F28.wireOp",EDGE,"E50.top"),sQuery(id+"F28.wireOp",EDGE,"E50.left"),subQ0])],"isStart":false})]}),makeQuery(id+"F40.opExtrude","SWEPT_EDGE",EDGE,{"disambiguationData":[OSD([subQ1,subQ0,sQuery(id+"F39.wireOp",EDGE,"E55"),sQuery(id+"F39.wireOp",EDGE,"E58")])]})]});}
            var Q5;
            {var subQ0=sQuery(id+"F31.wireOp",EDGE,"E51.right");var subQ2=sQuery(id+"F28.wireOp",EDGE,"E50.right");var subQ6=makeQuery(id+"F32.boolean.opBoolean","MERGE",EDGE,{"derivedFrom":[makeQuery(id+"F29.opExtrude","CAP_EDGE",EDGE,{"disambiguationData":[OSD([subQ2])],"isStart":true}),makeQuery(id+"F32.opExtrude","SWEPT_EDGE",EDGE,{"disambiguationData":[OSD([sQuery(id+"F31.wireOp",EDGE,"E51.top"),subQ0])]})]});Q5=makeQuery(id+"F38.boolean.opBoolean","MERGE",EDGE,{"derivedFrom":[makeQuery(id+"F35.boolean.opBoolean","SPLIT",EDGE,{"disambiguationData":[TD([makeQuery(id+"F30.opChamfer","BLEND_FACE",FACE,{"disambiguationData":[OSD([sQuery(id+"F28.wireOp",EDGE,"E50.bottom")])]})])],"derivedFrom":subQ6}),makeQuery(id+"F35.boolean.opBoolean","SPLIT",EDGE,{"disambiguationData":[TD([makeQuery(id+"F33.opChamfer","BLEND_FACE",FACE,{"disambiguationData":[OSD([sQuery(id+"F31.wireOp",EDGE,"E51.bottom")])]})])],"derivedFrom":subQ6}),makeQuery(id+"F38.opExtrude","CAP_EDGE",EDGE,{"disambiguationData":[OSD([sQuery(id+"F37.wireOp",EDGE,"E54.bottom")])],"isStart":true})]});}
            var Q6;
            {var subQ0=sQuery(id+"F31.wireOp",EDGE,"E51.left");var subQ2=sQuery(id+"F28.wireOp",EDGE,"E50.left");var subQ6=makeQuery(id+"F32.boolean.opBoolean","MERGE",EDGE,{"derivedFrom":[makeQuery(id+"F29.opExtrude","CAP_EDGE",EDGE,{"disambiguationData":[OSD([subQ2])],"isStart":true}),makeQuery(id+"F32.opExtrude","SWEPT_EDGE",EDGE,{"disambiguationData":[OSD([sQuery(id+"F31.wireOp",EDGE,"E51.top"),subQ0])]})]});Q6=makeQuery(id+"F38.boolean.opBoolean","MERGE",EDGE,{"derivedFrom":[makeQuery(id+"F35.boolean.opBoolean","SPLIT",EDGE,{"disambiguationData":[TD([makeQuery(id+"F30.opChamfer","BLEND_FACE",FACE,{"disambiguationData":[OSD([sQuery(id+"F28.wireOp",EDGE,"E50.bottom")])]})])],"derivedFrom":subQ6}),makeQuery(id+"F35.boolean.opBoolean","SPLIT",EDGE,{"disambiguationData":[TD([makeQuery(id+"F33.opChamfer","BLEND_FACE",FACE,{"disambiguationData":[OSD([sQuery(id+"F31.wireOp",EDGE,"E51.bottom")])]})])],"derivedFrom":subQ6}),makeQuery(id+"F38.opExtrude","CAP_EDGE",EDGE,{"disambiguationData":[OSD([sQuery(id+"F37.wireOp",EDGE,"E54.bottom")])],"isStart":false})]});}
            var Q7;
            Q7=makeQuery(id+"F30.opChamfer","BLEND_EDGE",EDGE,{"blendedFrom":[makeQuery(id+"F29.opExtrude","CAP_EDGE",EDGE,{"disambiguationData":[OSD([sQuery(id+"F28.wireOp",EDGE,"E50.bottom")])],"isStart":false}),makeQuery(id+"F1.opExtrude","SWEPT_FACE",FACE,{"disambiguationData":[OSD([sQuery(id+"F0.wireOp",EDGE,"E0.bottom")])]})],"blendedInto":[makeQuery(id+"F1.opExtrude","SWEPT_FACE",FACE,{"disambiguationData":[OSD([sQuery(id+"F0.wireOp",EDGE,"E0.bottom")])]})]});
            var Q8;
            Q8=makeQuery(id+"F33.opChamfer","BLEND_EDGE",EDGE,{"blendedFrom":[makeQuery(id+"F32.opExtrude","CAP_EDGE",EDGE,{"disambiguationData":[OSD([sQuery(id+"F31.wireOp",EDGE,"E51.bottom")])],"isStart":false}),makeQuery(id+"F1.opExtrude","SWEPT_FACE",FACE,{"disambiguationData":[OSD([sQuery(id+"F0.wireOp",EDGE,"E0.bottom")])]})],"blendedInto":[makeQuery(id+"F1.opExtrude","SWEPT_FACE",FACE,{"disambiguationData":[OSD([sQuery(id+"F0.wireOp",EDGE,"E0.bottom")])]})]});
            var Q9;
            Q9=makeQuery(id+"F33.opChamfer","BLEND_EDGE",EDGE,{"blendedFrom":[makeQuery(id+"F32.opExtrude","CAP_EDGE",EDGE,{"disambiguationData":[OSD([sQuery(id+"F31.wireOp",EDGE,"E51.bottom")])],"isStart":false}),makeQuery(id+"F32.boolean.opBoolean","MERGE",FACE,{"derivedFrom":[makeQuery(id+"F29.opExtrude","SWEPT_FACE",FACE,{"disambiguationData":[OSD([sQuery(id+"F28.wireOp",EDGE,"E50.left")])]}),makeQuery(id+"F32.opExtrude","SWEPT_FACE",FACE,{"disambiguationData":[OSD([sQuery(id+"F31.wireOp",EDGE,"E51.left")])]})]})],"blendedInto":[makeQuery(id+"F32.boolean.opBoolean","MERGE",FACE,{"derivedFrom":[makeQuery(id+"F29.opExtrude","SWEPT_FACE",FACE,{"disambiguationData":[OSD([sQuery(id+"F28.wireOp",EDGE,"E50.left")])]}),makeQuery(id+"F32.opExtrude","SWEPT_FACE",FACE,{"disambiguationData":[OSD([sQuery(id+"F31.wireOp",EDGE,"E51.left")])]})]})]});
            var Q10;
            Q10=makeQuery(id+"F33.opChamfer","BLEND_EDGE",EDGE,{"blendedFrom":[makeQuery(id+"F32.opExtrude","CAP_EDGE",EDGE,{"disambiguationData":[OSD([sQuery(id+"F31.wireOp",EDGE,"E51.bottom")])],"isStart":false}),makeQuery(id+"F32.boolean.opBoolean","MERGE",FACE,{"derivedFrom":[makeQuery(id+"F29.opExtrude","SWEPT_FACE",FACE,{"disambiguationData":[OSD([sQuery(id+"F28.wireOp",EDGE,"E50.right")])]}),makeQuery(id+"F32.opExtrude","SWEPT_FACE",FACE,{"disambiguationData":[OSD([sQuery(id+"F31.wireOp",EDGE,"E51.right")])]})]})],"blendedInto":[makeQuery(id+"F32.boolean.opBoolean","MERGE",FACE,{"derivedFrom":[makeQuery(id+"F29.opExtrude","SWEPT_FACE",FACE,{"disambiguationData":[OSD([sQuery(id+"F28.wireOp",EDGE,"E50.right")])]}),makeQuery(id+"F32.opExtrude","SWEPT_FACE",FACE,{"disambiguationData":[OSD([sQuery(id+"F31.wireOp",EDGE,"E51.right")])]})]})]});
            var Q11;
            {var subQ0=sQuery(id+"F31.wireOp",EDGE,"E51.bottom");Q11=makeQuery(id+"F33.opChamfer","BLEND_EDGE",EDGE,{"blendedFrom":[makeQuery(id+"F32.opExtrude","CAP_EDGE",EDGE,{"disambiguationData":[OSD([subQ0])],"isStart":false}),makeQuery(id+"F32.boolean.opBoolean","MERGE",FACE,{"derivedFrom":[makeQuery(id+"F29.opExtrude","CAP_FACE",FACE,{"disambiguationData":[OSD([sQuery(id+"F28.wireOp",EDGE,"E50.bottom"),sQuery(id+"F28.wireOp",EDGE,"E50.top"),sQuery(id+"F28.wireOp",EDGE,"E50.left"),sQuery(id+"F28.wireOp",EDGE,"E50.right")])],"isStart":false}),makeQuery(id+"F32.opExtrude","SWEPT_FACE",FACE,{"disambiguationData":[OSD([subQ0])]})]})],"blendedInto":[makeQuery(id+"F32.boolean.opBoolean","MERGE",FACE,{"derivedFrom":[makeQuery(id+"F29.opExtrude","CAP_FACE",FACE,{"disambiguationData":[OSD([sQuery(id+"F28.wireOp",EDGE,"E50.bottom"),sQuery(id+"F28.wireOp",EDGE,"E50.top"),sQuery(id+"F28.wireOp",EDGE,"E50.left"),sQuery(id+"F28.wireOp",EDGE,"E50.right")])],"isStart":false}),makeQuery(id+"F32.opExtrude","SWEPT_FACE",FACE,{"disambiguationData":[OSD([subQ0])]})]})]});}
            var Q12;
            Q12=makeQuery(id+"F32.boolean.opBoolean","MERGE",EDGE,{"derivedFrom":[makeQuery(id+"F29.opExtrude","CAP_EDGE",EDGE,{"disambiguationData":[OSD([sQuery(id+"F28.wireOp",EDGE,"E50.right")])],"isStart":false}),makeQuery(id+"F32.opExtrude","SWEPT_EDGE",EDGE,{"disambiguationData":[OSD([sQuery(id+"F31.wireOp",EDGE,"E51.bottom"),sQuery(id+"F31.wireOp",EDGE,"E51.right")])]})]});
            var Q13;
            Q13=makeQuery(id+"F32.boolean.opBoolean","MERGE",EDGE,{"derivedFrom":[makeQuery(id+"F29.opExtrude","CAP_EDGE",EDGE,{"disambiguationData":[OSD([sQuery(id+"F28.wireOp",EDGE,"E50.left")])],"isStart":false}),makeQuery(id+"F32.opExtrude","SWEPT_EDGE",EDGE,{"disambiguationData":[OSD([sQuery(id+"F31.wireOp",EDGE,"E51.bottom"),sQuery(id+"F31.wireOp",EDGE,"E51.left")])]})]});
            var Q14;
            Q14=makeQuery(id+"F40.opExtrude","CAP_EDGE",EDGE,{"disambiguationData":[OSD([sQuery(id+"F39.wireOp",EDGE,"E56.0")])],"isStart":false});
            var Q15;
            Q15=makeQuery(id+"F40.opExtrude","CAP_EDGE",EDGE,{"disambiguationData":[OSD([sQuery(id+"F39.wireOp",EDGE,"E56.0")])],"isStart":true});
            var Q16;
            {var subQ0=sQuery(id+"F34.wireOp",EDGE,"E53");Q16=makeQuery(id+"F35.boolean.opBoolean","SPLIT",EDGE,{"disambiguationData":[TD([makeQuery(id+"F29.opExtrude","SWEPT_FACE",FACE,{"disambiguationData":[OSD([sQuery(id+"F28.wireOp",EDGE,"E50.left")])]})])],"derivedFrom":makeQuery(id+"F35.opExtrude","CAP_EDGE",EDGE,{"disambiguationData":[OSD([subQ0])],"isStart":false})});}
            var Q17;
            {var subQ0=sQuery(id+"F34.wireOp",EDGE,"E53");var subQ1=makeQuery(id+"F35.opExtrude","SWEPT_FACE",FACE,{"disambiguationData":[OSD([subQ0])]});var subQ2=makeQuery(id+"F36.opExtrude","CAP_FACE",FACE,{"disambiguationData":[OSD([subQ0])],"isStart":false});Q17=makeQuery(id+"F36.boolean.opBoolean","COPY",EDGE,{"disambiguationData":[topologyDisambiguationEdgeConnected([subQ1,subQ2]),TD([makeQuery(id+"F29.opExtrude","SWEPT_FACE",FACE,{"disambiguationData":[OSD([sQuery(id+"F28.wireOp",EDGE,"E50.left")])]})])],"derivedFrom":makeQuery(id+"F36.opExtrude","CAP_EDGE",EDGE,{"disambiguationData":[OSD([subQ0])],"isStart":false})});}
            var Q18;
            Q18=makeQuery(id+"F35.boolean.opBoolean","INTERSECT",EDGE,{"derivedFrom":[makeQuery(id+"F32.boolean.opBoolean","MERGE",FACE,{"derivedFrom":[makeQuery(id+"F29.opExtrude","SWEPT_FACE",FACE,{"disambiguationData":[OSD([sQuery(id+"F28.wireOp",EDGE,"E50.left")])]}),makeQuery(id+"F32.opExtrude","SWEPT_FACE",FACE,{"disambiguationData":[OSD([sQuery(id+"F31.wireOp",EDGE,"E51.left")])]})]}),makeQuery(id+"F35.opExtrude","CAP_FACE",FACE,{"disambiguationData":[OSD([sQuery(id+"F34.wireOp",EDGE,"E53")])],"isStart":false})]});
            var Q19;
            Q19=makeQuery(id+"F38.opExtrude","CAP_EDGE",EDGE,{"disambiguationData":[OSD([sQuery(id+"F37.wireOp",EDGE,"E54.top")])],"isStart":false});
            var Q20;
            Q20=makeQuery(id+"F35.boolean.opBoolean","INTERSECT",EDGE,{"derivedFrom":[makeQuery(id+"F32.boolean.opBoolean","MERGE",FACE,{"derivedFrom":[makeQuery(id+"F29.opExtrude","SWEPT_FACE",FACE,{"disambiguationData":[OSD([sQuery(id+"F28.wireOp",EDGE,"E50.right")])]}),makeQuery(id+"F32.opExtrude","SWEPT_FACE",FACE,{"disambiguationData":[OSD([sQuery(id+"F31.wireOp",EDGE,"E51.right")])]})]}),makeQuery(id+"F35.opExtrude","CAP_FACE",FACE,{"disambiguationData":[OSD([sQuery(id+"F34.wireOp",EDGE,"E53")])],"isStart":false})]});
            var Q21;
            Q21=makeQuery(id+"F38.opExtrude","CAP_EDGE",EDGE,{"disambiguationData":[OSD([sQuery(id+"F37.wireOp",EDGE,"E54.top")])],"isStart":true});
            var Q22;
            {var subQ0=sQuery(id+"F34.wireOp",EDGE,"E53");Q22=makeQuery(id+"F35.boolean.opBoolean","SPLIT",EDGE,{"disambiguationData":[TD([makeQuery(id+"F29.opExtrude","SWEPT_FACE",FACE,{"disambiguationData":[OSD([sQuery(id+"F28.wireOp",EDGE,"E50.right")])]})])],"derivedFrom":makeQuery(id+"F35.opExtrude","CAP_EDGE",EDGE,{"disambiguationData":[OSD([subQ0])],"isStart":false})});}
            var Q23;
            {var subQ0=sQuery(id+"F34.wireOp",EDGE,"E53");var subQ1=makeQuery(id+"F35.opExtrude","SWEPT_FACE",FACE,{"disambiguationData":[OSD([subQ0])]});var subQ2=makeQuery(id+"F36.opExtrude","CAP_FACE",FACE,{"disambiguationData":[OSD([subQ0])],"isStart":false});Q23=makeQuery(id+"F36.boolean.opBoolean","COPY",EDGE,{"disambiguationData":[topologyDisambiguationEdgeConnected([subQ1,subQ2]),TD([makeQuery(id+"F29.opExtrude","SWEPT_FACE",FACE,{"disambiguationData":[OSD([sQuery(id+"F28.wireOp",EDGE,"E50.right")])]})])],"derivedFrom":makeQuery(id+"F36.opExtrude","CAP_EDGE",EDGE,{"disambiguationData":[OSD([subQ0])],"isStart":false})});}
            fillet(context, id + "F46", {"entities" : qUnion([Q0, Q1, Q2, Q3, Q4, Q5, Q6, Q7, Q8, Q9, Q10, Q11, Q12, Q13, Q14, Q15, Q16, Q17, Q18, Q19, Q20, Q21, Q22, Q23]), "radius" : 8 * mm, "tangentPropagation" : true, "allowEdgeOverflow" : false});
        }
        {
            var Q0;
            Q0=makeQuery(id+"F40.opExtrude","CAP_EDGE",EDGE,{"disambiguationData":[OSD([sQuery(id+"F39.wireOp",EDGE,"E57")])],"isStart":false});
            var Q1;
            Q1=makeQuery(id+"F40.opExtrude","SWEPT_EDGE",EDGE,{"disambiguationData":[OSD([sQuery(id+"F39.wireOp",EDGE,"E55"),sQuery(id+"F39.wireOp",EDGE,"E57")])]});
            var Q2;
            Q2=makeQuery(id+"F40.opExtrude","CAP_EDGE",EDGE,{"disambiguationData":[OSD([sQuery(id+"F39.wireOp",EDGE,"E57")])],"isStart":true});
            var Q3;
            Q3=makeQuery(id+"F40.opExtrude","SWEPT_EDGE",EDGE,{"disambiguationData":[OSD([sQuery(id+"F39.wireOp",EDGE,"E56.0"),sQuery(id+"F39.wireOp",EDGE,"E57")])]});
            fillet(context, id + "F47", {"entities" : qUnion([Q0, Q1, Q2, Q3]), "radius" : 8 * mm, "tangentPropagation" : true, "allowEdgeOverflow" : false});
        }
        {
            var Q0;
            {var subQ0=sQuery(id+"F4.wireOp",EDGE,"E5.left");var subQ2=sQuery(id+"F4.wireOp",EDGE,"E5.bottom");var subQ6=makeQuery(id+"F5.opExtrude","CAP_EDGE",EDGE,{"disambiguationData":[OSD([subQ0])],"isStart":false});Q0=makeQuery(id+"F15.boolean.opBoolean","MERGE",EDGE,{"derivedFrom":[makeQuery(id+"F12.boolean.opBoolean","SPLIT",EDGE,{"disambiguationData":[TD([makeQuery(id+"F5.opExtrude","SWEPT_FACE",FACE,{"disambiguationData":[OSD([subQ2])]})])],"derivedFrom":subQ6}),makeQuery(id+"F12.boolean.opBoolean","SPLIT",EDGE,{"disambiguationData":[TD([makeQuery(id+"F8.boolean.opBoolean","COPY",FACE,{"derivedFrom":makeQuery(id+"F8.opExtrude","SWEPT_FACE",FACE,{"disambiguationData":[OSD([sQuery(id+"F7.wireOp",EDGE,"E9")])]})})])],"derivedFrom":subQ6}),makeQuery(id+"F15.opExtrude","CAP_EDGE",EDGE,{"disambiguationData":[OSD([sQuery(id+"F14.wireOp",EDGE,"E27")])],"isStart":true})]});}
            var Q1;
            Q1=makeQuery(id+"F5.opExtrude","CAP_EDGE",EDGE,{"disambiguationData":[OSD([sQuery(id+"F4.wireOp",EDGE,"E5.right")])],"isStart":false});
            var Q2;
            {var subQ0=sQuery(id+"F4.wireOp",EDGE,"E5.right");Q2=makeQuery(id+"F6.opFillet","BLEND_EDGE",EDGE,{"blendedFrom":[makeQuery(id+"F5.boolean.opBoolean","INTERSECT",EDGE,{"derivedFrom":[makeQuery(id+"F3.boolean.opBoolean","COPY",FACE,{"derivedFrom":makeQuery(id+"F3.opExtrude","SWEPT_FACE",FACE,{"disambiguationData":[OSD([sQuery(id+"F2.wireOp",EDGE,"E3")])]})}),makeQuery(id+"F5.opExtrude","SWEPT_FACE",FACE,{"disambiguationData":[OSD([subQ0])]})]}),makeQuery(id+"F5.opExtrude","CAP_FACE",FACE,{"disambiguationData":[OSD([sQuery(id+"F4.wireOp",EDGE,"E5.bottom"),sQuery(id+"F4.wireOp",EDGE,"E5.top"),sQuery(id+"F4.wireOp",EDGE,"E5.left"),subQ0])],"isStart":false})],"blendedInto":[makeQuery(id+"F5.opExtrude","CAP_FACE",FACE,{"disambiguationData":[OSD([sQuery(id+"F4.wireOp",EDGE,"E5.bottom"),sQuery(id+"F4.wireOp",EDGE,"E5.top"),sQuery(id+"F4.wireOp",EDGE,"E5.left"),subQ0])],"isStart":false})]});}
            var Q3;
            Q3=makeQuery(id+"F6.opFillet","BLEND_EDGE",EDGE,{"blendedFrom":[makeQuery(id+"F3.boolean.opBoolean","COPY",EDGE,{"derivedFrom":makeQuery(id+"F3.opExtrude","CAP_EDGE",EDGE,{"disambiguationData":[OSD([sQuery(id+"F2.wireOp",EDGE,"E3")])],"isStart":false})}),makeQuery(id+"F1.opExtrude","SWEPT_FACE",FACE,{"disambiguationData":[OSD([sQuery(id+"F0.wireOp",EDGE,"E0.top")])]})],"blendedInto":[makeQuery(id+"F1.opExtrude","SWEPT_FACE",FACE,{"disambiguationData":[OSD([sQuery(id+"F0.wireOp",EDGE,"E0.top")])]})]});
            var Q4;
            Q4=makeQuery(id+"F3.boolean.opBoolean","COPY",EDGE,{"derivedFrom":makeQuery(id+"F3.opExtrude","CAP_EDGE",EDGE,{"disambiguationData":[OSD([sQuery(id+"F0.wireOp",EDGE,"E0.top"),sQuery(id+"F0.wireOp",EDGE,"E0.right")])],"isStart":false})});
            var Q5;
            {var subQ0=sQuery(id+"F0.wireOp",EDGE,"E0.left");var subQ2=sQuery(id+"F0.wireOp",EDGE,"E0.top");var subQ4=makeQuery(id+"F1.opExtrude","SWEPT_EDGE",EDGE,{"disambiguationData":[OSD([subQ2,subQ0])]});Q5=makeQuery(id+"F20.boolean.opBoolean","MERGE",EDGE,{"derivedFrom":[makeQuery(id+"F17.boolean.opBoolean","SPLIT",EDGE,{"disambiguationData":[TD([makeQuery(id+"F5.opExtrude","SWEPT_FACE",FACE,{"disambiguationData":[OSD([sQuery(id+"F4.wireOp",EDGE,"E5.bottom")])]})])],"derivedFrom":subQ4}),makeQuery(id+"F17.boolean.opBoolean","SPLIT",EDGE,{"disambiguationData":[TD([makeQuery(id+"F8.boolean.opBoolean","COPY",FACE,{"derivedFrom":makeQuery(id+"F8.opExtrude","SWEPT_FACE",FACE,{"disambiguationData":[OSD([sQuery(id+"F7.wireOp",EDGE,"E9")])]})})])],"derivedFrom":subQ4}),makeQuery(id+"F20.opExtrude","CAP_EDGE",EDGE,{"disambiguationData":[OSD([sQuery(id+"F19.wireOp",EDGE,"E37")])],"isStart":true})]});}
            var Q6;
            {var subQ2=sQuery(id+"F0.wireOp",EDGE,"E0.bottom");var subQ3=sQuery(id+"F0.wireOp",EDGE,"E0.right");Q6=makeQuery(id+"F43.boolean.opBoolean","SPLIT",EDGE,{"disambiguationData":[TD([makeQuery(id+"F5.opExtrude","SWEPT_FACE",FACE,{"disambiguationData":[OSD([sQuery(id+"F4.wireOp",EDGE,"E5.bottom")])]})])],"derivedFrom":makeQuery(id+"F1.opExtrude","SWEPT_EDGE",EDGE,{"disambiguationData":[OSD([subQ2,subQ3])]})});}
            var Q7;
            Q7=makeQuery(id+"F1.opExtrude","CAP_EDGE",EDGE,{"disambiguationData":[OSD([sQuery(id+"F0.wireOp",EDGE,"E0.bottom")])],"isStart":false});
            var Q8;
            {var subQ0=sQuery(id+"F4.wireOp",EDGE,"E5.left");var subQ1=sQuery(id+"F4.wireOp",EDGE,"E5.bottom");var subQ2=sQuery(id+"F0.wireOp",EDGE,"E0.right");var subQ5=sQuery(id+"F0.wireOp",EDGE,"E0.bottom");var subQ8=makeQuery(id+"F5.boolean.opBoolean","MERGE",EDGE,{"derivedFrom":[makeQuery(id+"F1.opExtrude","CAP_EDGE",EDGE,{"disambiguationData":[OSD([subQ2])],"isStart":false}),makeQuery(id+"F5.opExtrude","SWEPT_EDGE",EDGE,{"disambiguationData":[OSD([subQ1,subQ0])]})]});Q8=makeQuery(id+"F13.boolean.opBoolean","MERGE",EDGE,{"derivedFrom":[makeQuery(id+"F12.boolean.opBoolean","SPLIT",EDGE,{"disambiguationData":[TD([makeQuery(id+"F1.opExtrude","SWEPT_FACE",FACE,{"disambiguationData":[OSD([subQ5])]})])],"derivedFrom":subQ8}),makeQuery(id+"F12.boolean.opBoolean","SPLIT",EDGE,{"disambiguationData":[TD([makeQuery(id+"F12.opExtrude","SWEPT_FACE",FACE,{"disambiguationData":[OSD([sQuery(id+"F11.wireOp",EDGE,"E25")])]})])],"derivedFrom":subQ8}),makeQuery(id+"F13.opExtrude","CAP_EDGE",EDGE,{"disambiguationData":[OSD([sQuery(id+"F11.wireOp",EDGE,"E20"),sQuery(id+"F11.wireOp",EDGE,"E26")])],"isStart":true})]});}
            var Q9;
            Q9=makeQuery(id+"F5.opExtrude","SWEPT_EDGE",EDGE,{"disambiguationData":[OSD([sQuery(id+"F0.wireOp",EDGE,"E0.bottom"),sQuery(id+"F4.wireOp",EDGE,"E5.bottom"),sQuery(id+"F4.wireOp",EDGE,"E5.right")])]});
            var Q10;
            Q10=makeQuery(id+"F6.opFillet","BLEND_EDGE",EDGE,{"blendedFrom":[makeQuery(id+"F5.boolean.opBoolean","INTERSECT",EDGE,{"derivedFrom":[makeQuery(id+"F3.boolean.opBoolean","COPY",FACE,{"derivedFrom":makeQuery(id+"F3.opExtrude","SWEPT_FACE",FACE,{"disambiguationData":[OSD([sQuery(id+"F2.wireOp",EDGE,"E3")])]})}),makeQuery(id+"F5.opExtrude","SWEPT_FACE",FACE,{"disambiguationData":[OSD([sQuery(id+"F4.wireOp",EDGE,"E5.right")])]})]}),makeQuery(id+"F5.boolean.opBoolean","MERGE",FACE,{"derivedFrom":[makeQuery(id+"F1.opExtrude","CAP_FACE",FACE,{"disambiguationData":[OSD([sQuery(id+"F0.wireOp",EDGE,"E0.bottom"),sQuery(id+"F0.wireOp",EDGE,"E0.top"),sQuery(id+"F0.wireOp",EDGE,"E0.left"),sQuery(id+"F0.wireOp",EDGE,"E0.right")])],"isStart":false}),makeQuery(id+"F5.opExtrude","SWEPT_FACE",FACE,{"disambiguationData":[OSD([sQuery(id+"F4.wireOp",EDGE,"E5.bottom")])]})]})],"blendedInto":[makeQuery(id+"F5.boolean.opBoolean","MERGE",FACE,{"derivedFrom":[makeQuery(id+"F1.opExtrude","CAP_FACE",FACE,{"disambiguationData":[OSD([sQuery(id+"F0.wireOp",EDGE,"E0.bottom"),sQuery(id+"F0.wireOp",EDGE,"E0.top"),sQuery(id+"F0.wireOp",EDGE,"E0.left"),sQuery(id+"F0.wireOp",EDGE,"E0.right")])],"isStart":false}),makeQuery(id+"F5.opExtrude","SWEPT_FACE",FACE,{"disambiguationData":[OSD([sQuery(id+"F4.wireOp",EDGE,"E5.bottom")])]})]})]});
            var Q11;
            Q11=makeQuery(id+"F3.boolean.opBoolean","COPY",EDGE,{"derivedFrom":makeQuery(id+"F3.opExtrude","CAP_EDGE",EDGE,{"disambiguationData":[OSD([sQuery(id+"F0.wireOp",EDGE,"E0.right")])],"isStart":false})});
            var Q12;
            Q12=makeQuery(id+"F1.opExtrude","CAP_EDGE",EDGE,{"disambiguationData":[OSD([sQuery(id+"F0.wireOp",EDGE,"E0.top")])],"isStart":false});
            var Q13;
            {var subQ0=sQuery(id+"F0.wireOp",EDGE,"E0.left");var subQ2=sQuery(id+"F0.wireOp",EDGE,"E0.top");var subQ4=sQuery(id+"F0.wireOp",EDGE,"E0.bottom");var subQ7=makeQuery(id+"F1.opExtrude","CAP_EDGE",EDGE,{"disambiguationData":[OSD([subQ0])],"isStart":false});Q13=makeQuery(id+"F18.boolean.opBoolean","MERGE",EDGE,{"derivedFrom":[makeQuery(id+"F17.boolean.opBoolean","SPLIT",EDGE,{"disambiguationData":[TD([makeQuery(id+"F1.opExtrude","SWEPT_FACE",FACE,{"disambiguationData":[OSD([subQ4])]})])],"derivedFrom":subQ7}),makeQuery(id+"F17.boolean.opBoolean","SPLIT",EDGE,{"disambiguationData":[TD([makeQuery(id+"F1.opExtrude","SWEPT_FACE",FACE,{"disambiguationData":[OSD([subQ2])]})])],"derivedFrom":subQ7}),makeQuery(id+"F18.opExtrude","CAP_EDGE",EDGE,{"disambiguationData":[OSD([sQuery(id+"F16.wireOp",EDGE,"E30"),sQuery(id+"F16.wireOp",EDGE,"E36")])],"isStart":true})]});}
            var Q14;
            {var subQ0=sQuery(id+"F0.wireOp",EDGE,"E0.left");var subQ2=sQuery(id+"F0.wireOp",EDGE,"E0.bottom");Q14=makeQuery(id+"F43.boolean.opBoolean","SPLIT",EDGE,{"disambiguationData":[TD([makeQuery(id+"F5.opExtrude","SWEPT_FACE",FACE,{"disambiguationData":[OSD([sQuery(id+"F4.wireOp",EDGE,"E5.bottom")])]})])],"derivedFrom":makeQuery(id+"F1.opExtrude","SWEPT_EDGE",EDGE,{"disambiguationData":[OSD([subQ2,subQ0])]})});}
            fillet(context, id + "F48", {"entities" : qUnion([Q0, Q1, Q2, Q3, Q4, Q5, Q6, Q7, Q8, Q9, Q10, Q11, Q12, Q13, Q14]), "radius" : 10 * mm, "tangentPropagation" : true, "allowEdgeOverflow" : false});
        }
        {
            var Q0;
            Q0=makeQuery(id+"F5.opExtrude","CAP_EDGE",EDGE,{"disambiguationData":[OSD([sQuery(id+"F4.wireOp",EDGE,"E5.bottom")])],"isStart":false});
            fillet(context, id + "F49", {"entities" : qUnion([Q0]), "radius" : 10 * mm, "tangentPropagation" : true, "allowEdgeOverflow" : false});
        }
        {
            var Q0;
            Q0=makeQuery(id+"F26.opExtrude","CAP_EDGE",EDGE,{"disambiguationData":[OSD([sQuery(id+"F25.wireOp",EDGE,"E43.bottom")])],"isStart":false});
            var Q1;
            Q1=makeQuery(id+"F26.opExtrude","CAP_EDGE",EDGE,{"disambiguationData":[OSD([sQuery(id+"F25.wireOp",EDGE,"E43.top")])],"isStart":false});
            var Q2;
            Q2=makeQuery(id+"F26.opExtrude","CAP_EDGE",EDGE,{"disambiguationData":[OSD([sQuery(id+"F25.wireOp",EDGE,"E43.right")])],"isStart":false});
            var Q3;
            Q3=makeQuery(id+"F26.opExtrude","CAP_EDGE",EDGE,{"disambiguationData":[OSD([sQuery(id+"F25.wireOp",EDGE,"E43.left")])],"isStart":false});
            fillet(context, id + "F50", {"entities" : qUnion([Q0, Q1, Q2, Q3]), "radius" : 10 * mm, "tangentPropagation" : true, "allowEdgeOverflow" : false});
        }
    });
